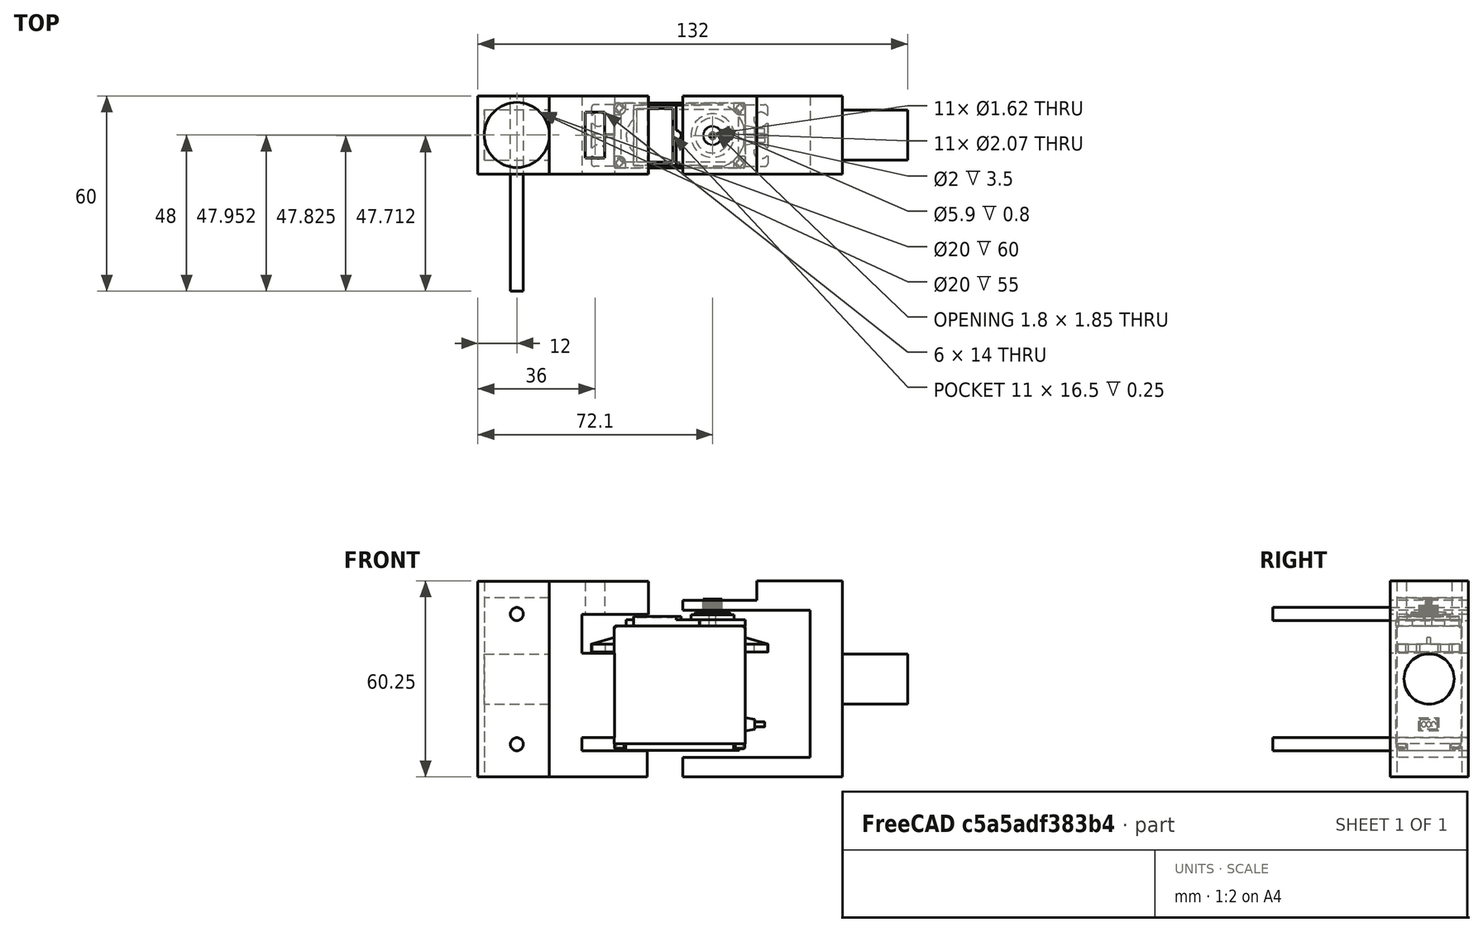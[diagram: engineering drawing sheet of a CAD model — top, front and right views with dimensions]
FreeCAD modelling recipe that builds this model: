
FCSTD DOCUMENT  (FreeCAD 0.21R33771 (Git))
Label: U_Servo_conjunto_angulo
License: All rights reserved
LicenseURL: http://en.wikipedia.org/wiki/All_rights_reserved
objects: Sketcher::SketchObject×7, PartDesign::Pad×5, PartDesign::Body×3, Part::Cylinder×3, PartDesign::Pocket×2, Mesh::Feature×1, Part::Feature×1, Part::Box×1, PartDesign::FeatureBase×1, Part::Cut×1, App::DocumentObjectGroup×1
note: 31 computed .brp shape members not serialized (recipe doc carries the construction recipe); baked Part::Feature solids carry a one-line shape summary decoded from their .brp

FEATURE [Mesh::Feature] servo_lower_cover_fake_shaft
  Placement = pos=(0,-12,2) rot=(0,1,0;3.14159rad)
FEATURE [Part::Feature] Part__Feature  label="MG996R"
  Placement = pos=(0,-9,-0.5) rot=(0,0,1;0rad)
  shape: bbox 54.21 x 20.13 x 46.64 mm, 453 faces, 11 solids (baked)
FEATURE [Sketcher::SketchObject] Sketch
  FullyConstrained = false
  MapMode = 5
  Placement = pos=(0,0,0) rot=(1,0,0;1.5708rad)
  Support = -> [XZ_Plane]
  sketch-geometry (12):
    g0: LineSegment StartX=-9.57792 StartY=39.9337 StartZ=0 EndX=-30 EndY=39.9337 EndZ=0
    g1: LineSegment StartX=-9.57792 StartY=50 StartZ=0 EndX=-40 EndY=50 EndZ=0
    g2: LineSegment StartX=-20 StartY=28 StartZ=0 EndX=-30 EndY=28 EndZ=0
    g3: LineSegment StartX=-20 StartY=2.0296 StartZ=0 EndX=-30 EndY=2.0296 EndZ=0
    g4: LineSegment StartX=-40 StartY=-10 StartZ=0 EndX=-9.99258 EndY=-10 EndZ=0
    g5: LineSegment StartX=-9.99258 StartY=-2 StartZ=0 EndX=-30 EndY=-2 EndZ=0
    g6: LineSegment StartX=-40 StartY=50 StartZ=0 EndX=-40 EndY=-10 EndZ=0
    g7: LineSegment StartX=-9.99258 StartY=-10 StartZ=0 EndX=-9.99258 EndY=-2 EndZ=0
    g8: LineSegment StartX=-30 StartY=-2 StartZ=0 EndX=-30 EndY=2.0296 EndZ=0
    g9: LineSegment StartX=-20 StartY=28 StartZ=0 EndX=-20 EndY=2.0296 EndZ=0
    g10: LineSegment StartX=-30 StartY=28 StartZ=0 EndX=-30 EndY=39.9337 EndZ=0
    g11: LineSegment StartX=-9.57792 StartY=39.9337 StartZ=0 EndX=-9.57792 EndY=50 EndZ=0
  constraints (24):
    c: Horizontal(g0)
    c: Horizontal(g1)
    c: Horizontal(g2)
    c: Horizontal(g3)
    c: Horizontal(g4)
    c: Horizontal(g5)
    c: Coincident(g6,g1)
    c: Coincident(g6,g4)
    c: Vertical(g6)
    c: Coincident(g7,g4)
    c: Coincident(g7,g5)
    c: Vertical(g7)
    c: Coincident(g8,g5)
    c: Coincident(g8,g3)
    c: Vertical(g8)
    c: Coincident(g9,g2)
    c: Coincident(g9,g3)
    c: Vertical(g9)
    c: Coincident(g10,g2)
    c: Coincident(g10,g0)
    c: Vertical(g10)
    c: Coincident(g11,g0)
    c: Coincident(g11,g1)
    c: Vertical(g11)
FEATURE [PartDesign::Pad] Pad
  Direction = (0,-1,-2e-16)
  Length = 24
  Length2 = 10
  Placement = pos=(0,0,0) rot=(1,0,0;1.5708rad)
  Profile = -> Sketch
  ReferenceAxis = -> Sketch [N_Axis]
  Type = 0
FEATURE [Sketcher::SketchObject] Sketch001
  FullyConstrained = false
  MapMode = 5
  Placement = pos=(0,-1.11e-14,50) rot=(0,0,1;3.14159rad)
  Support = -> [Pad]
  sketch-geometry (4):
    g0: LineSegment StartX=23 StartY=19.048 StartZ=0 EndX=29 EndY=19.048 EndZ=0
    g1: LineSegment StartX=29 StartY=19.048 StartZ=0 EndX=29 EndY=5.04802 EndZ=0
    g2: LineSegment StartX=29 StartY=5.04802 StartZ=0 EndX=23 EndY=5.04802 EndZ=0
    g3: LineSegment StartX=23 StartY=5.04802 StartZ=0 EndX=23 EndY=19.048 EndZ=0
  constraints (8):
    c: Coincident(g0,g1)
    c: Coincident(g1,g2)
    c: Coincident(g2,g3)
    c: Coincident(g3,g0)
    c: Horizontal(g0)
    c: Horizontal(g2)
    c: Vertical(g1)
    c: Vertical(g3)
FEATURE [Sketcher::SketchObject] Sketch002
  FullyConstrained = false
  MapMode = 5
  Placement = pos=(-40,0,0) rot=(0.707107,0,-0.707107;3.14159rad)
  sketch-geometry (1):
    g0: Circle CenterX=-20 CenterY=12 CenterZ=0 NormalX=0 NormalY=0 NormalZ=1 AngleXU=0 Radius=7.73291
FEATURE [PartDesign::Pad] Pad001
  BaseFeature = -> Pad
  Direction = (-1,0,-2e-16)
  Length = 20
  Length2 = 10
  Placement = pos=(0,0,0) rot=(1,0,0;1.5708rad)
  Profile = -> Sketch002
  ReferenceAxis = -> Sketch002 [N_Axis]
  Type = 0
FEATURE [PartDesign::Pocket] Pocket
  BaseFeature = -> Pad001
  Direction = (0,2e-16,-1)
  Length = 11
  Length2 = 5
  Placement = pos=(0,0,0) rot=(1,0,0;1.5708rad)
  Profile = -> Sketch001
  ReferenceAxis = -> Sketch001 [N_Axis]
  Type = 0
FEATURE [PartDesign::Body] Body  label="T_bracket_redondo"
  Group = -> [Sketch,Pad,Sketch001,Sketch002,Pad001,Pocket]
  Origin = -> Origin
  Tip = -> Pocket
FEATURE [Sketcher::SketchObject] Sketch003
  FullyConstrained = false
  MapMode = 5
  Placement = pos=(0,0,0) rot=(1,0,0;1.5708rad)
  Support = -> [XZ_Plane001]
  sketch-geometry (10):
    g0: LineSegment StartX=1.01714 StartY=-4.08621 StartZ=0 EndX=40.1359 EndY=-4.08621 EndZ=0
    g1: LineSegment StartX=1.01714 StartY=-10.0633 StartZ=0 EndX=50 EndY=-10.0633 EndZ=0
    g2: LineSegment StartX=40.1359 StartY=-4.08621 StartZ=0 EndX=40.1359 EndY=41.1434 EndZ=0
    g3: LineSegment StartX=40.1359 StartY=41.1434 StartZ=0 EndX=1.00976 EndY=41.1434 EndZ=0
    g4: LineSegment StartX=1.00976 StartY=44.2323 StartZ=0 EndX=23.6784 EndY=44.2323 EndZ=0
    g5: LineSegment StartX=23.6784 StartY=50.1921 StartZ=0 EndX=50 EndY=50.1921 EndZ=0
    g6: LineSegment StartX=50 StartY=-10.0633 StartZ=0 EndX=50 EndY=50.1921 EndZ=0
    g7: LineSegment StartX=1.00976 StartY=44.2323 StartZ=0 EndX=1.00976 EndY=41.1434 EndZ=0
    g8: LineSegment StartX=23.6784 StartY=50.1921 StartZ=0 EndX=23.6784 EndY=44.2323 EndZ=0
    g9: LineSegment StartX=1.01714 StartY=-4.08621 StartZ=0 EndX=1.01714 EndY=-10.0633 EndZ=0
  constraints (20):
    c: Horizontal(g0)
    c: Horizontal(g1)
    c: Coincident(g2,g0)
    c: Vertical(g2)
    c: Coincident(g3,g2)
    c: Horizontal(g3)
    c: Horizontal(g4)
    c: Horizontal(g5)
    c: Coincident(g6,g1)
    c: Coincident(g6,g5)
    c: Vertical(g6)
    c: Coincident(g7,g4)
    c: Coincident(g7,g3)
    c: Vertical(g7)
    c: Coincident(g8,g5)
    c: Coincident(g8,g4)
    c: Vertical(g8)
    c: Coincident(g9,g0)
    c: Coincident(g9,g1)
    c: Vertical(g9)
FEATURE [PartDesign::Pad] Pad002
  Direction = (0,-1,2e-16)
  Length = 24
  Length2 = 10
  Placement = pos=(0,0,0) rot=(1,0,0;1.5708rad)
  Profile = -> Sketch003
  ReferenceAxis = -> Sketch003 [N_Axis]
  Type = 0
FEATURE [Sketcher::SketchObject] Sketch004
  FullyConstrained = false
  MapMode = 5
  Placement = pos=(50,0,0) rot=(0.707107,0,0.707107;3.14159rad)
  Support = -> [Pad002]
  sketch-geometry (1):
    g0: Circle CenterX=20.0454 CenterY=12.0314 CenterZ=0 NormalX=0 NormalY=0 NormalZ=1 AngleXU=0 Radius=7.70236
FEATURE [PartDesign::Pad] Pad003
  BaseFeature = -> Pad002
  Direction = (1,0,-2e-16)
  Length = 20
  Length2 = 10
  Placement = pos=(0,0,0) rot=(1,0,0;1.5708rad)
  Profile = -> Sketch004
  ReferenceAxis = -> Sketch004 [N_Axis]
  Type = 0
FEATURE [PartDesign::Body] Body001  label="U_redondo"
  Group = -> [Sketch003,Pad002,Sketch004,Pad003]
  Origin = -> Origin001
  Tip = -> Pad003
FEATURE [Sketcher::SketchObject] Sketch005
  FullyConstrained = false
  MapMode = 5
  Placement = pos=(0,0,0) rot=(1,0,0;1.5708rad)
  Support = -> [XZ_Plane002]
  sketch-geometry (12):
    g0: LineSegment StartX=-9.57792 StartY=39.9337 StartZ=0 EndX=-30 EndY=39.9337 EndZ=0
    g1: LineSegment StartX=-9.57792 StartY=50 StartZ=0 EndX=-40 EndY=50 EndZ=0
    g2: LineSegment StartX=-20 StartY=28 StartZ=0 EndX=-30 EndY=28 EndZ=0
    g3: LineSegment StartX=-20 StartY=2.0296 StartZ=0 EndX=-30 EndY=2.0296 EndZ=0
    g4: LineSegment StartX=-40 StartY=-10 StartZ=0 EndX=-9.99258 EndY=-10 EndZ=0
    g5: LineSegment StartX=-9.99258 StartY=-2 StartZ=0 EndX=-30 EndY=-2 EndZ=0
    g6: LineSegment StartX=-40 StartY=50 StartZ=0 EndX=-40 EndY=-10 EndZ=0
    g7: LineSegment StartX=-9.99258 StartY=-10 StartZ=0 EndX=-9.99258 EndY=-2 EndZ=0
    g8: LineSegment StartX=-30 StartY=-2 StartZ=0 EndX=-30 EndY=2.0296 EndZ=0
    g9: LineSegment StartX=-20 StartY=28 StartZ=0 EndX=-20 EndY=2.0296 EndZ=0
    g10: LineSegment StartX=-30 StartY=28 StartZ=0 EndX=-30 EndY=39.9337 EndZ=0
    g11: LineSegment StartX=-9.57792 StartY=39.9337 StartZ=0 EndX=-9.57792 EndY=50 EndZ=0
  constraints (24):
    c: Horizontal(g0)
    c: Horizontal(g1)
    c: Horizontal(g2)
    c: Horizontal(g3)
    c: Horizontal(g4)
    c: Horizontal(g5)
    c: Coincident(g6,g1)
    c: Coincident(g6,g4)
    c: Vertical(g6)
    c: Coincident(g7,g4)
    c: Coincident(g7,g5)
    c: Vertical(g7)
    c: Coincident(g8,g5)
    c: Coincident(g8,g3)
    c: Vertical(g8)
    c: Coincident(g9,g2)
    c: Coincident(g9,g3)
    c: Vertical(g9)
    c: Coincident(g10,g2)
    c: Coincident(g10,g0)
    c: Vertical(g10)
    c: Coincident(g11,g0)
    c: Coincident(g11,g1)
    c: Vertical(g11)
FEATURE [Part::Cylinder] Cylinder  label="Cilindro"
  Angle = 360
  AttacherType = Attacher::AttachEngine3D
  FirstAngle = 0
  Height = 60
  Placement = pos=(-50,-12,-15) rot=(0,0,1;0rad)
  Radius = 10
  SecondAngle = 0
FEATURE [Part::Box] Box  label="Cubo"
  AttacherType = Attacher::AttachEngine3D
  Height = 60
  Length = 22
  Placement = pos=(-62,-24,-10) rot=(0,0,1;0rad)
  Width = 24
FEATURE [PartDesign::FeatureBase] BaseFeature
FEATURE [PartDesign::Pad] Pad004
  BaseFeature = -> BaseFeature
  Direction = (0,-1,-2e-16)
  Length = 24
  Length2 = 10
  Profile = -> Sketch005
  ReferenceAxis = -> Sketch005 [N_Axis]
  Type = 0
FEATURE [Sketcher::SketchObject] Sketch006
  FullyConstrained = false
  MapMode = 5
  Placement = pos=(0,4e-16,-2) rot=(0,0,1;0rad)
  Support = -> [Pad004]
  sketch-geometry (4):
    g0: LineSegment StartX=23 StartY=19.048 StartZ=0 EndX=29 EndY=19.048 EndZ=0
    g1: LineSegment StartX=29 StartY=19.048 StartZ=0 EndX=29 EndY=5.04802 EndZ=0
    g2: LineSegment StartX=29 StartY=5.04802 StartZ=0 EndX=23 EndY=5.04802 EndZ=0
    g3: LineSegment StartX=23 StartY=5.04802 StartZ=0 EndX=23 EndY=19.048 EndZ=0
  constraints (8):
    c: Coincident(g0,g1)
    c: Coincident(g1,g2)
    c: Coincident(g2,g3)
    c: Coincident(g3,g0)
    c: Horizontal(g0)
    c: Horizontal(g2)
    c: Vertical(g1)
    c: Vertical(g3)
FEATURE [PartDesign::Pocket] Pocket001
  BaseFeature = -> Pad004
  Direction = (0,2e-16,-1)
  Length = 11
  Length2 = 5
  Profile = -> Sketch006
  ReferenceAxis = -> Sketch006 [N_Axis]
  Type = 0
FEATURE [PartDesign::Body] Body002  label="T_bracket_abrazo"
  Group = -> [BaseFeature,Sketch005,Pad004,Sketch006,Pocket001]
  Origin = -> Origin002
  Tip = -> Pocket001
FEATURE [Part::Cylinder] Cylinder001  label="Cilindro001"
  Angle = 360
  AttacherType = Attacher::AttachEngine3D
  FirstAngle = 0
  Height = 60
  Placement = pos=(-50,0,0) rot=(1,0,0;1.5708rad)
  Radius = 2
  SecondAngle = 0
FEATURE [Part::Cylinder] Cylinder002  label="Cilindro002"
  Angle = 360
  AttacherType = Attacher::AttachEngine3D
  FirstAngle = 0
  Height = 60
  Placement = pos=(-50,0,40) rot=(1,0,0;1.5708rad)
  Radius = 2
  SecondAngle = 0
FEATURE [Part::Cut] Cut
  Base = -> Box
  Tool = -> Cylinder
FEATURE [App::DocumentObjectGroup] Group  label="T_abrazo"
  Group = -> [Cut,Cylinder002,Cylinder001,Body002]
